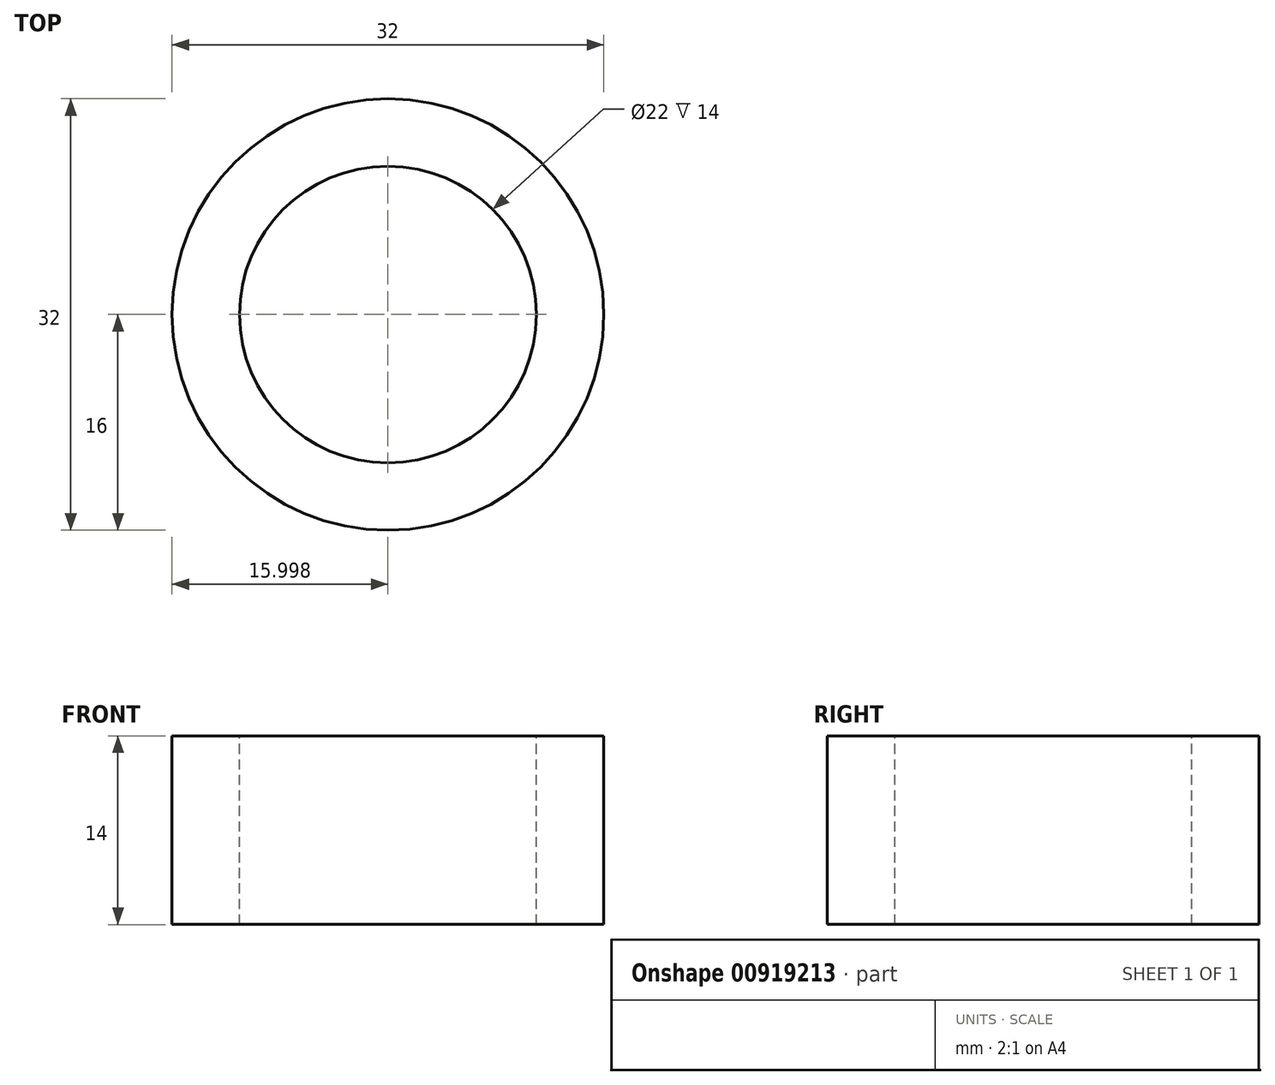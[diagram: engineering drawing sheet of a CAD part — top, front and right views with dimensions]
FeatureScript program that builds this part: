
annotation { "Feature Type Name" : "Feature", "Feature Type Description" : "" }
export const myFeature = defineFeature(function(context is Context, id is Id, definition is map)
    precondition{}
    {
        {
            var Q0;
            Q0=qCreatedBy(makeId("Front.planeOp"),FACE);
            var sketch = newSketch(context, id + "F0", { "sketchPlane" : qUnion([Q0])});
            skLineSegment(sketch, "E0", {"start": v(-75.33, 43.37) * mm, "end": v(-75.33, -33.3) * mm, "construction": true});
            skLineSegment(sketch, "E1", {"start": v(-75.33, -23.54) * mm, "end": v(-91.33, -23.54) * mm});
            skLineSegment(sketch, "E2", {"start": v(-91.33, -23.54) * mm, "end": v(-91.33, -9.54) * mm});
            skLineSegment(sketch, "E3", {"start": v(-91.33, -9.54) * mm, "end": v(-75.33, -9.54) * mm});
            skLineSegment(sketch, "E4.0", {"start": v(-86.33, -23.54) * mm, "end": v(-86.33, -9.54) * mm});
            skSolve(sketch);
        }
        {
            var Q0;
            {var subQ0=sQuery(id+"F0.wireOp",EDGE,"E2");Q0=makeQuery(id+"F0.imprint","IMPRINT",FACE,{"disambiguationData":[TD([[makeQuery(id+"F0.imprint","IMPRINT",EDGE,{"derivedFrom":subQ0}),-1.0]])]});}
            var Q1;
            Q1=sQuery(id+"F0.wireOp",EDGE,"E0");
            revolve(context, id + "F1", {"surfaceOperationType" : NewSurfaceOperationType.NEW, "entities" : qUnion([Q0]), "axis" : qUnion([Q1]), "revolveType" : RevolveType.FULL});
        }
    });
